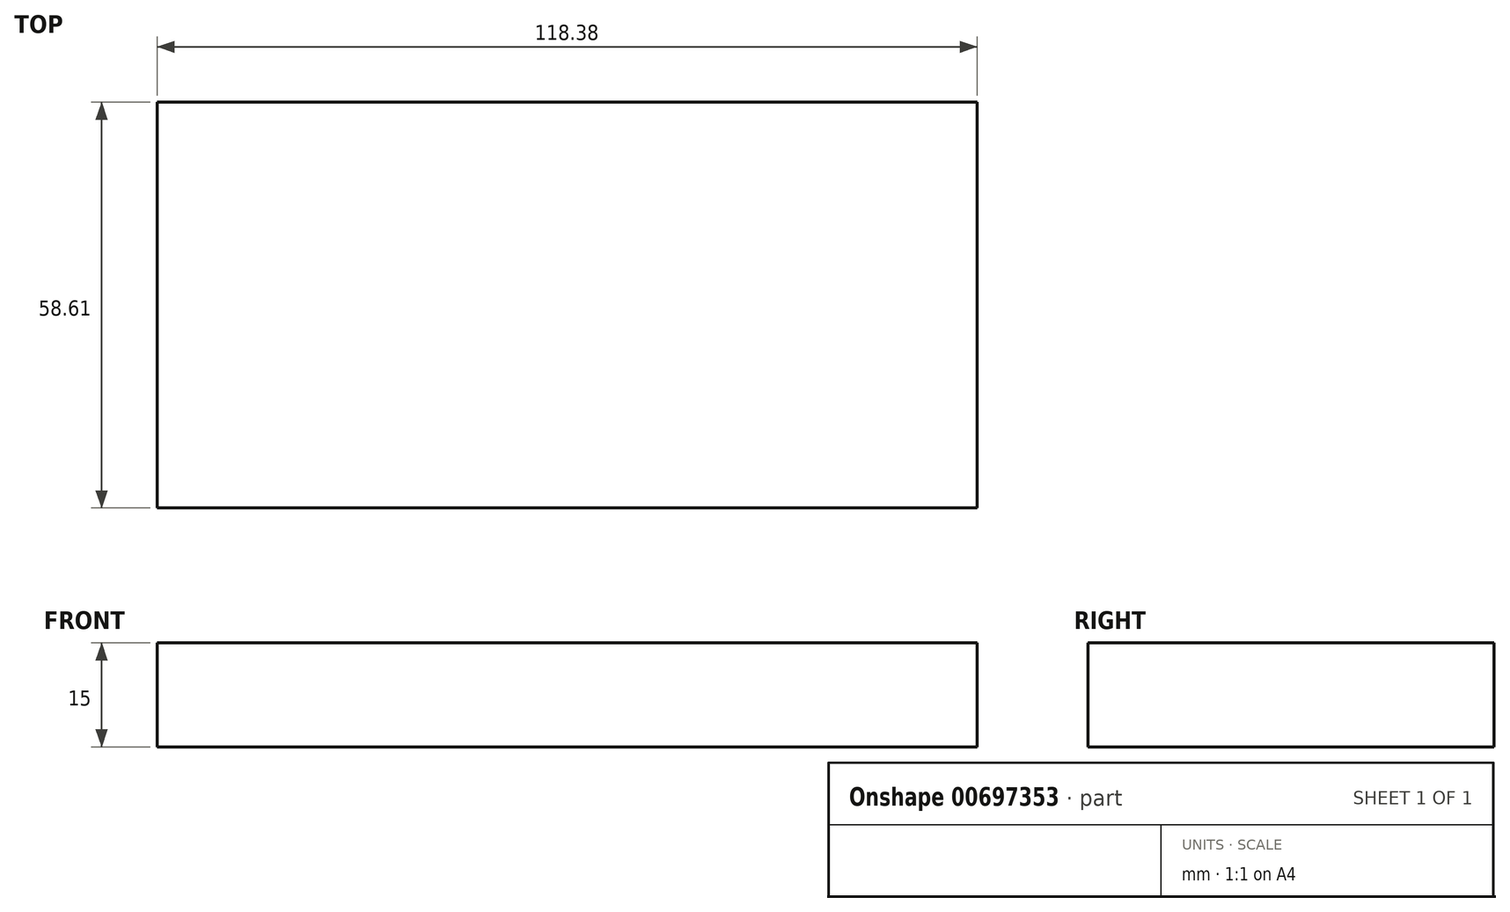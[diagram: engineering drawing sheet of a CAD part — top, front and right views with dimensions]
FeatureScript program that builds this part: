
annotation { "Feature Type Name" : "Feature", "Feature Type Description" : "" }
export const myFeature = defineFeature(function(context is Context, id is Id, definition is map)
    precondition{}
    {
        {
            var Q0;
            Q0=qCreatedBy(makeId("Top.planeOp"),FACE);
            var sketch = newSketch(context, id + "F0", { "sketchPlane" : qUnion([Q0])});
            skLineSegment(sketch, "E0.bottom", {"start": v(-47.53, -18.03) * mm, "end": v(70.85, -18.03) * mm});
            skLineSegment(sketch, "E0.top", {"start": v(-47.53, 40.58) * mm, "end": v(70.85, 40.58) * mm});
            skLineSegment(sketch, "E0.left", {"start": v(-47.53, -18.03) * mm, "end": v(-47.53, 40.58) * mm});
            skLineSegment(sketch, "E0.right", {"start": v(70.85, -18.03) * mm, "end": v(70.85, 40.58) * mm});
            skSolve(sketch);
        }
        {
            var Q0;
            Q0 = qSketchRegion(id + "F0", true);
            extrude(context, id + "F1", {"entities" : qUnion([Q0]), "depth" : 15 * mm, "offsetDistance" : 25 * mm});
        }
    });
